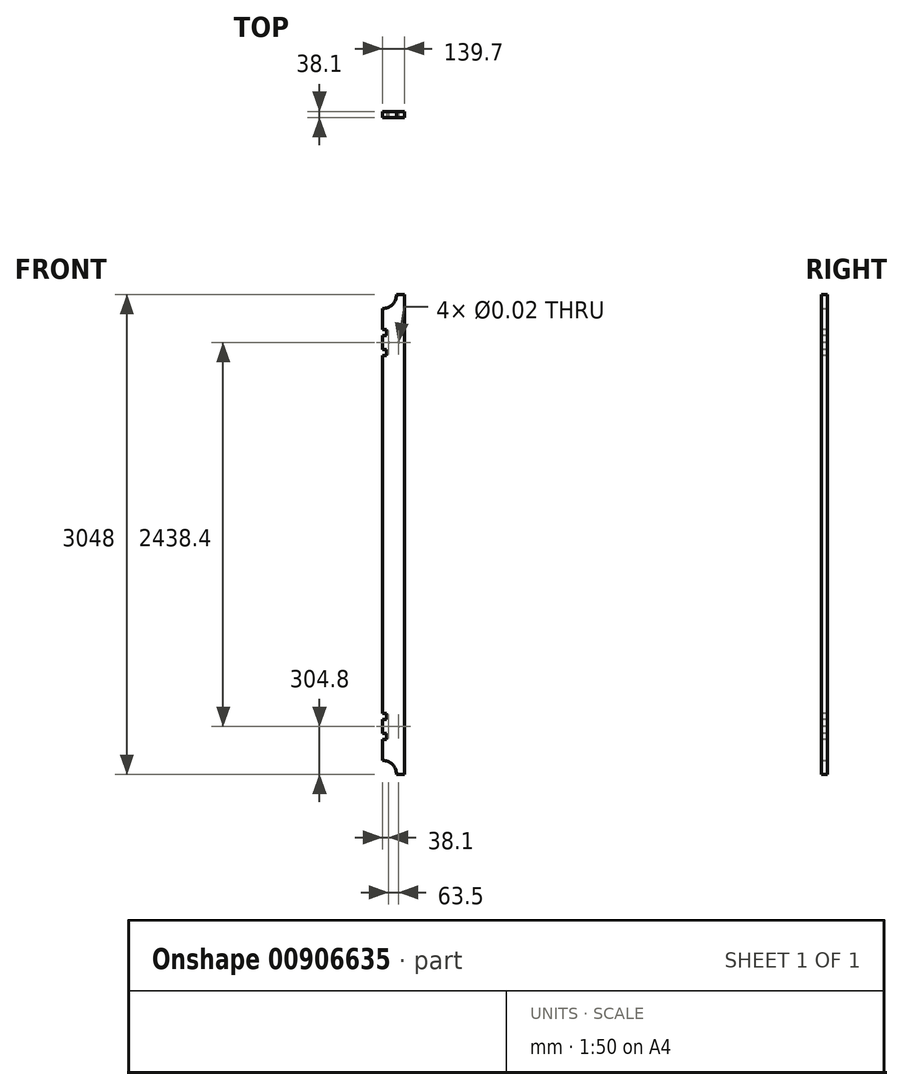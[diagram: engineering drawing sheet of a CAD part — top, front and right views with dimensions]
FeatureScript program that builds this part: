
annotation { "Feature Type Name" : "Feature", "Feature Type Description" : "" }
export const myFeature = defineFeature(function(context is Context, id is Id, definition is map)
    precondition{}
    {
        {
            var Q0;
            Q0=qCreatedBy(makeId("Front.planeOp"),FACE);
            var sketch = newSketch(context, id + "F0", { "sketchPlane" : qUnion([Q0])});
            skLineSegment(sketch, "E0", {"start": v(0, -88.9) * mm, "end": v(0, -2959.1) * mm});
            skLineSegment(sketch, "E1", {"start": v(88.9, -3048) * mm, "end": v(139.7, -3048) * mm});
            skLineSegment(sketch, "E2", {"start": v(139.7, -3048) * mm, "end": v(139.7, 0) * mm});
            skLineSegment(sketch, "E3", {"start": v(139.7, 0) * mm, "end": v(88.9, 0) * mm});
            skArc(sketch, "E4", {"start": v(0, -88.9) * mm, "mid": v(62.86, -62.86) * mm, "end": v(88.9, 0) * mm});
            skArc(sketch, "E5", {"start": v(88.9, -3048) * mm, "mid": v(62.86, -2985.14) * mm, "end": v(0, -2959.1) * mm});
            skSolve(sketch);
        }
        {
            var Q0;
            Q0=makeQuery(id+"F0.imprint","IMPRINT",FACE,{"disambiguationData":[TD([[makeQuery(id+"F0.imprint","IMPRINT",EDGE,{"derivedFrom":sQuery(id+"F0.wireOp",EDGE,"E0")}),1.0]])]});
            extrude(context, id + "F1", {"entities" : qUnion([Q0]), "depth" : 38.1 * mm, "offsetDistance" : 25.4 * mm});
        }
        {
            var Q0;
            Q0=makeQuery(id+"F1.opExtrude","CAP_FACE",FACE,{"disambiguationData":[OSD([sQuery(id+"F0.wireOp",EDGE,"E0"),sQuery(id+"F0.wireOp",EDGE,"E1"),sQuery(id+"F0.wireOp",EDGE,"E2"),sQuery(id+"F0.wireOp",EDGE,"E3"),sQuery(id+"F0.wireOp",EDGE,"E4"),sQuery(id+"F0.wireOp",EDGE,"E5")])],"isStart":false});
            var sketch = newSketch(context, id + "F2", { "sketchPlane" : qUnion([Q0])});
            skCircle(sketch, "E6", {"center": v(101.6, -304.8) * mm, "radius": 6.35 * mm});
            skCircle(sketch, "E7", {"center": v(38.1, -304.8) * mm, "radius": 6.35 * mm});
            skCircle(sketch, "E8", {"center": v(101.6, -2743.2) * mm, "radius": 6.35 * mm});
            skCircle(sketch, "E9", {"center": v(38.1, -2743.2) * mm, "radius": 6.35 * mm});
            skSolve(sketch);
        }
        {
            var Q0;
            Q0=sQuery(id+"F2.wireOp",VERTEX,"E9.center");
            var Q1;
            Q1=sQuery(id+"F2.wireOp",VERTEX,"E8.center");
            var Q2;
            Q2=sQuery(id+"F2.wireOp",VERTEX,"E7.center");
            var Q3;
            Q3=sQuery(id+"F2.wireOp",VERTEX,"E6.center");
            var Q4;
            Q4=makeQuery(id+"F1.opExtrude","SWEPT_BODY",BODY,{"disambiguationData":[OSD([sQuery(id+"F0.wireOp",EDGE,"E0"),sQuery(id+"F0.wireOp",EDGE,"E1"),sQuery(id+"F0.wireOp",EDGE,"E2"),sQuery(id+"F0.wireOp",EDGE,"E3"),sQuery(id+"F0.wireOp",EDGE,"E4"),sQuery(id+"F0.wireOp",EDGE,"E5")])]});
            hole(context, id + "F3", {"style" : HoleStyle.SIMPLE, "endStyle" : HoleEndStyle.THROUGH, "standardTappedOrClearance" : lookupTablePath({ "standard" : "ANSI", "size" : "1/2 (0.5)", "type" : "Drilled" }), "standardBlindInLast" : lookupTablePath({ "standard" : "ANSI", "size" : "1/2", "type" : "Drilled" }), "holeDiameter" : 1 / 50.8 * mm, "majorDiameter" : 6.35 * mm, "isTappedThrough" : true, "tappedDepth" : 10.3 * mm, "tapClearance" : 3, "startFromSketch" : true, "locations" : qUnion([Q0, Q1, Q2, Q3]), "scope" : qUnion([Q4])});
        }
        {
            var Q0;
            Q0=makeQuery(id+"F1.opExtrude","CAP_FACE",FACE,{"disambiguationData":[OSD([sQuery(id+"F0.wireOp",EDGE,"E0"),sQuery(id+"F0.wireOp",EDGE,"E1"),sQuery(id+"F0.wireOp",EDGE,"E2"),sQuery(id+"F0.wireOp",EDGE,"E3"),sQuery(id+"F0.wireOp",EDGE,"E4"),sQuery(id+"F0.wireOp",EDGE,"E5")])],"isStart":false});
            var sketch = newSketch(context, id + "F4", { "sketchPlane" : qUnion([Q0])});
            skLineSegment(sketch, "E10", {"start": v(101.6, -304.8) * mm, "end": v(0, -304.8) * mm});
            skLineSegment(sketch, "E11", {"start": v(0, -304.8) * mm, "end": v(0, -260.35) * mm});
            skLineSegment(sketch, "E12", {"start": v(0, -260.35) * mm, "end": v(25.4, -260.35) * mm});
            skLineSegment(sketch, "E13", {"start": v(25.4, -260.35) * mm, "end": v(25.4, -222.25) * mm});
            skLineSegment(sketch, "E14", {"start": v(25.4, -222.25) * mm, "end": v(0, -222.25) * mm});
            skLineSegment(sketch, "E15", {"start": v(0, -304.8) * mm, "end": v(0, -349.25) * mm});
            skLineSegment(sketch, "E16", {"start": v(0, -349.25) * mm, "end": v(25.4, -349.25) * mm});
            skLineSegment(sketch, "E17", {"start": v(25.4, -349.25) * mm, "end": v(25.4, -387.35) * mm});
            skLineSegment(sketch, "E18", {"start": v(25.4, -387.35) * mm, "end": v(0, -387.35) * mm});
            skLineSegment(sketch, "E19", {"start": v(101.6, -2743.2) * mm, "end": v(0, -2743.2) * mm});
            skLineSegment(sketch, "E20", {"start": v(0, -2743.2) * mm, "end": v(0, -2698.75) * mm});
            skLineSegment(sketch, "E21", {"start": v(0, -2698.75) * mm, "end": v(25.4, -2698.75) * mm});
            skLineSegment(sketch, "E22", {"start": v(25.4, -2698.75) * mm, "end": v(25.4, -2660.65) * mm});
            skLineSegment(sketch, "E23", {"start": v(25.4, -2660.65) * mm, "end": v(0, -2660.65) * mm});
            skLineSegment(sketch, "E24", {"start": v(0, -2743.2) * mm, "end": v(0, -2787.65) * mm});
            skLineSegment(sketch, "E25", {"start": v(0, -2787.65) * mm, "end": v(25.4, -2787.65) * mm});
            skLineSegment(sketch, "E26", {"start": v(25.4, -2787.65) * mm, "end": v(25.4, -2825.75) * mm});
            skLineSegment(sketch, "E27", {"start": v(25.4, -2825.75) * mm, "end": v(0, -2825.75) * mm});
            skSolve(sketch);
        }
        {
            var Q0;
            {var subQ0=sQuery(id+"F4.wireOp",EDGE,"E12");Q0=makeQuery(id+"F4.imprint","IMPRINT",FACE,{"disambiguationData":[TD([[makeQuery(id+"F4.imprint","IMPRINT",EDGE,{"derivedFrom":subQ0}),1.0]])]});}
            var Q1;
            {var subQ0=sQuery(id+"F4.wireOp",EDGE,"E16");Q1=makeQuery(id+"F4.imprint","IMPRINT",FACE,{"disambiguationData":[TD([[makeQuery(id+"F4.imprint","IMPRINT",EDGE,{"derivedFrom":subQ0}),-1.0]])]});}
            var Q2;
            {var subQ0=sQuery(id+"F4.wireOp",EDGE,"E21");Q2=makeQuery(id+"F4.imprint","IMPRINT",FACE,{"disambiguationData":[TD([[makeQuery(id+"F4.imprint","IMPRINT",EDGE,{"derivedFrom":subQ0}),1.0]])]});}
            var Q3;
            {var subQ0=sQuery(id+"F4.wireOp",EDGE,"E25");Q3=makeQuery(id+"F4.imprint","IMPRINT",FACE,{"disambiguationData":[TD([[makeQuery(id+"F4.imprint","IMPRINT",EDGE,{"derivedFrom":subQ0}),-1.0]])]});}
            extrude(context, id + "F5", {"entities" : qUnion([Q0, Q1, Q2, Q3]), "operationType" : NewBodyOperationType.REMOVE, "endBound" : BoundingType.THROUGH_ALL, "oppositeDirection" : true, "depth" : 25.4 * mm, "offsetDistance" : 25.4 * mm});
        }
    });
